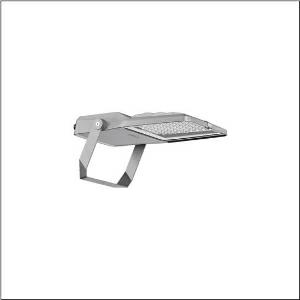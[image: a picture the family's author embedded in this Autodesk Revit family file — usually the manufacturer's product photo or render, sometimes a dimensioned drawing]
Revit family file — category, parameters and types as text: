
# Revit family: floodlight_fl_21_mini___pl64_5xa7775d2e1a_23e2
name_source: partatom
category: Lighting Fixtures
units: mm (PartAtom-declared; Revit-internal decimal feet)

## family parameters
Cut with Voids When Loaded = No
Host = Face
Light Source = No
Part Type = Normal
Room Calculation Point = No
Round Connector Dimension = Use Diameter
Shared = No

## types (1)
- --- (1 x LED, 17220 lm, 142.9 W, 3000K)
    Apparent Load = 143 VA
    CIE Flux Codes = 28 80 98 100 100
    Color Rendering = 70
    Color Temperature = 3000K
    Default Elevation = 1800 mm
    Description = Floodlight FL 21 mini, floodlight, primary light control with lens, of PMMA, primary optical cover: protective disc, of toughened safety glass, transparent, light distribution: PL64, light emission: direct distribution, installation type: surface-mounted, LED, High Power LED, rated luminous flux: 17.220lm, luminous efficacy: 121lm/W, light colour: 730, colour temperature: 3000K, control gear: Smart Interface (Zhaga), control: flexible luminous flux parameterisation, time-dependent luminous flux control, constant luminous flux control, overheat protection, pre-setting: logarithmic dimming characteristic, with terminal, 6-pole, mains connection: 220..240V, AC, 50/60Hz, start of lifetime: 143W, end of service life: 151W, reduction: 63W, luminaire housing, of diecast aluminium, powder-coated, Siteco® metallic grey (DB 702S), corrosivity category C5 mid according to DIN EN ISO 12944, suitable for swimming pools, chlorine-resistant, sealing non-destructively replaceable, mounting bracket, of steel, galvanised, powder-coated, Siteco® metallic grey (DB 702S), Smart Interface above, protection rating (complete): IP66, insulation class (complete): insulation class II (safety insulation), certification: CE, ENEC, VDE, protection symbol: D, impact resistance: IK08, permissible operating ambient temperature: -40..+40°C, permissible operating ambient temperature for outdoor applications: -40..+50°C, standard: DIN EN 12944, LABS conformity tested according to VDMA 24364:2018-05, packaging unit: 1 piece

Light Distribution: PL64
    Height = 70 mm
    Lamp = 1 x LED
    Lamp Light Flux = 17220 lm
    Lamp Power = 142.9 W
    Lamp count = 1
    Length = 485 mm
    Luminous efficacy = 121 lm/W
    Manufacturer = Siteco
    ModVariant = No
    Model = 5XA7775D2E1A
    Number of Poles = 1
    OnlyDefault = Yes
    Power Factor = 1
    Product Name = Floodlight FL 21 mini | PL64
    Product group = floodlight | pylon annexe
    ProductGroupID = 6200
    Protection Class = Protection class II
    Protection Degree = IP 66
    RLX_Detail_Level = 1
    RLX_Emergency_Light_Flux = 0 lm
    RLX_Emergency_Type = 0
    RLX_Emergency_Type_DB = No
    RlxData = <blob elided: 96337 chars, md5=493154a4>
    Socket = socket
    Standby Power = 0 W
    System Light Flux = 17220 lm
    System Power = 143 W
    Type Comments = factory setting: luminous flux: 100 % | dim-lin: 254 | 730 mA
    Type Image = l_1006845.jpg
    URL = http://relux.com
    VarID = @adj_165312
    Voltage = 0 V
    Weight = 0.00 kg
    Width = 337 mm

## geometry (parser evidence)
native form markers: Blend x4, Sweep x11
no freeform markers — native parametric forms only
